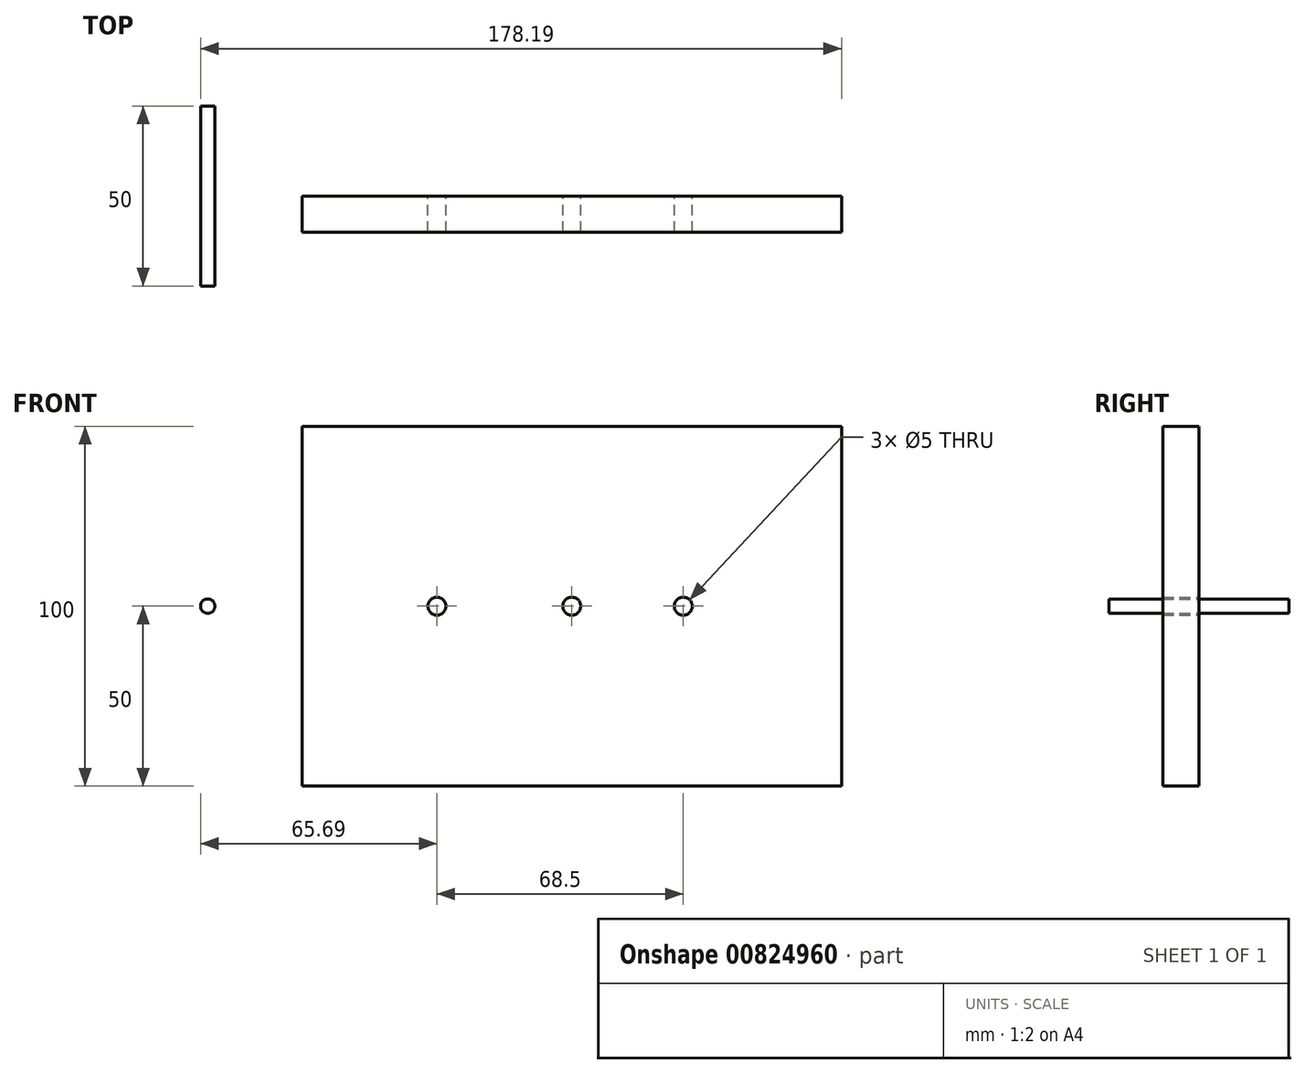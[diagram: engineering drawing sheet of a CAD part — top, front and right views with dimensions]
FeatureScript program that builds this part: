
annotation { "Feature Type Name" : "Feature", "Feature Type Description" : "" }
export const myFeature = defineFeature(function(context is Context, id is Id, definition is map)
    precondition{}
    {
        {
            var Q0;
            Q0=qCreatedBy(makeId("Front.planeOp"),FACE);
            var sketch = newSketch(context, id + "F0", { "sketchPlane" : qUnion([Q0])});
            skLineSegment(sketch, "E0.bottom", {"start": v(-75, 50) * mm, "end": v(75, 50) * mm});
            skLineSegment(sketch, "E0.top", {"start": v(-75, -50) * mm, "end": v(75, -50) * mm});
            skLineSegment(sketch, "E0.left", {"start": v(-75, 50) * mm, "end": v(-75, -50) * mm});
            skLineSegment(sketch, "E0.right", {"start": v(75, 50) * mm, "end": v(75, -50) * mm});
            skPoint(sketch, "E0.middle", {"position": v(0, 0) * mm});
            skCircle(sketch, "E1", {"center": v(-37.5, 0) * mm, "radius": 2.5 * mm});
            skCircle(sketch, "E2", {"center": v(0, 0) * mm, "radius": 2.5 * mm});
            skCircle(sketch, "E3", {"center": v(31, 0) * mm, "radius": 2.5 * mm});
            skSolve(sketch);
        }
        {
            var Q0;
            Q0=makeQuery(id+"F0.imprint","IMPRINT",FACE,{"disambiguationData":[TD([[makeQuery(id+"F0.imprint","IMPRINT",EDGE,{"derivedFrom":sQuery(id+"F0.wireOp",EDGE,"E0.bottom")}),-1.0]])]});
            extrude(context, id + "F1", {"entities" : qUnion([Q0]), "depth" : 10 * mm, "offsetDistance" : 25 * mm});
        }
        {
            var Q0;
            Q0=qCreatedBy(makeId("Front.planeOp"),FACE);
            var sketch = newSketch(context, id + "F2", { "sketchPlane" : qUnion([Q0])});
            skCircle(sketch, "E4", {"center": v(-101.2, 0) * mm, "radius": 2 * mm});
            skSolve(sketch);
        }
        {
            var Q0;
            Q0 = qSketchRegion(id + "F2", true);
            extrude(context, id + "F3", {"entities" : qUnion([Q0]), "operationType" : NewBodyOperationType.ADD, "endBound" : BoundingType.SYMMETRIC, "depth" : 50 * mm, "offsetDistance" : 25 * mm});
        }
    });
